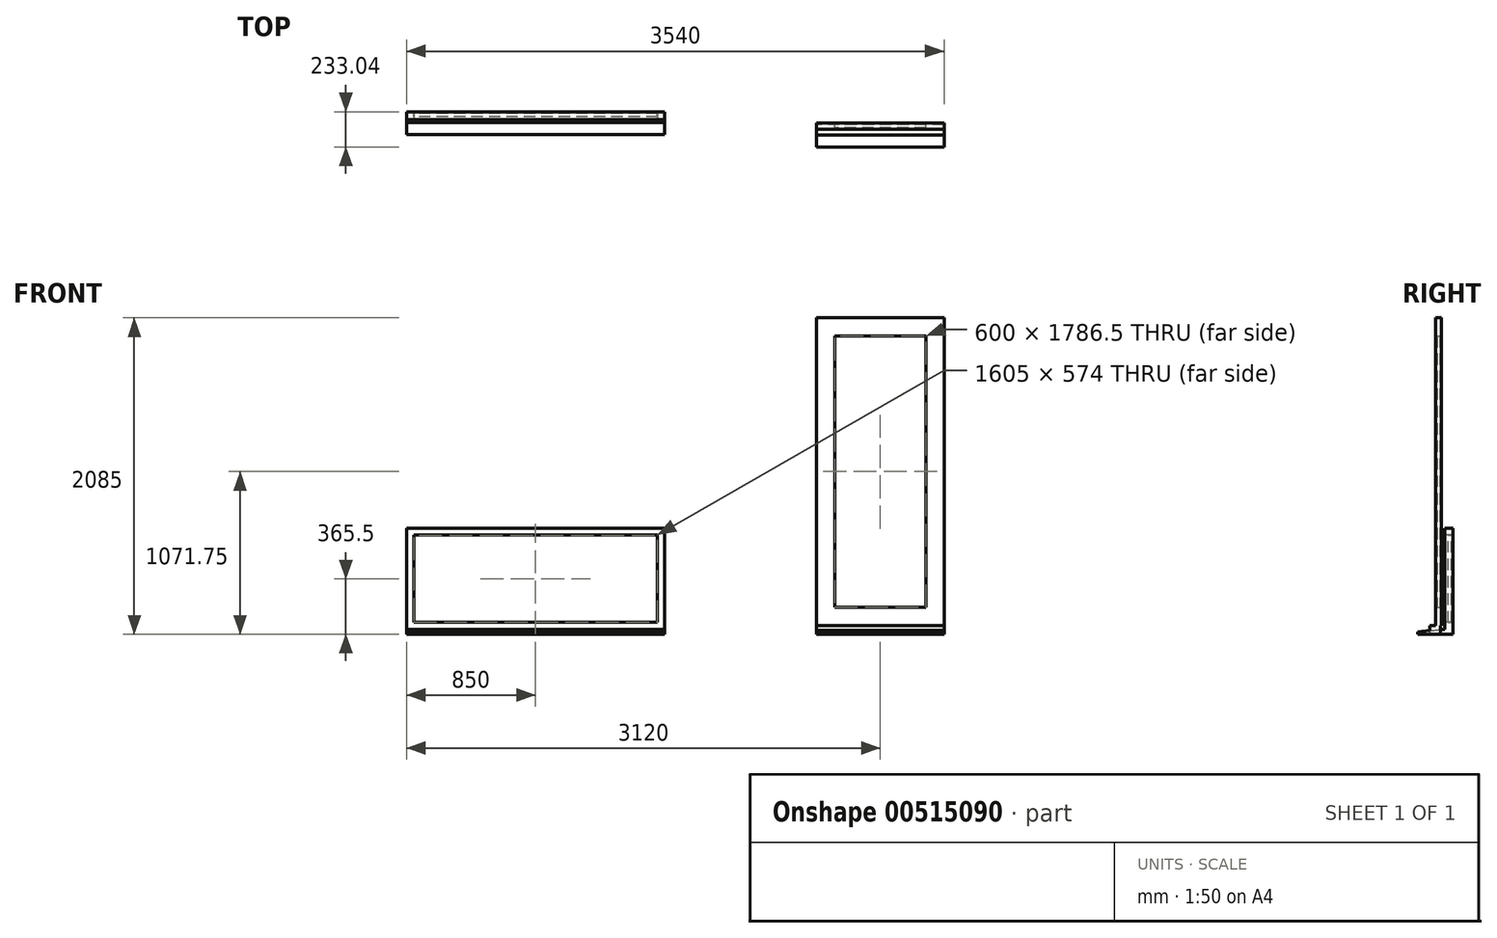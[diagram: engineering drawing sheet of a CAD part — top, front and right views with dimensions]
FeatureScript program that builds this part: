
annotation { "Feature Type Name" : "Feature", "Feature Type Description" : "" }
export const myFeature = defineFeature(function(context is Context, id is Id, definition is map)
    precondition{}
    {
        {
            var Q0;
            Q0=qCreatedBy(makeId("Right.planeOp"),FACE);
            var sketch = newSketch(context, id + "F0", { "sketchPlane" : qUnion([Q0])});
            skLineSegment(sketch, "E0.bottom", {"start": v(83.04, 0) * mm, "end": v(-66.96, 0) * mm});
            skLineSegment(sketch, "E0.top", {"start": v(83.04, 31) * mm, "end": v(-66.96, 31) * mm});
            skLineSegment(sketch, "E0.left", {"start": v(83.04, 0) * mm, "end": v(83.04, 31) * mm});
            skLineSegment(sketch, "E0.right", {"start": v(-66.96, 0) * mm, "end": v(-66.96, 31) * mm});
            skSolve(sketch);
        }
        {
            var Q0;
            Q0=makeQuery(id+"F0.imprint","IMPRINT",FACE,{"disambiguationData":[TD([[makeQuery(id+"F0.imprint","IMPRINT",EDGE,{"derivedFrom":sQuery(id+"F0.wireOp",EDGE,"E0.bottom")}),-1.0]])]});
            extrude(context, id + "F1", {"entities" : qUnion([Q0]), "oppositeDirection" : true, "depth" : 1700 * mm});
        }
        {
            var Q0;
            Q0=makeQuery(id+"F1.opExtrude","SWEPT_FACE",FACE,{"disambiguationData":[OSD([sQuery(id+"F0.wireOp",EDGE,"E0.left")])]});
            var sketch = newSketch(context, id + "F2", { "sketchPlane" : qUnion([Q0])});
            skLineSegment(sketch, "E1.bottom", {"start": v(0, 31) * mm, "end": v(1700, 31) * mm});
            skLineSegment(sketch, "E1.top", {"start": v(0, 700) * mm, "end": v(1700, 700) * mm});
            skLineSegment(sketch, "E1.left", {"start": v(0, 31) * mm, "end": v(0, 700) * mm});
            skLineSegment(sketch, "E1.right", {"start": v(1700, 31) * mm, "end": v(1700, 700) * mm});
            skSolve(sketch);
        }
        {
            var Q0;
            Q0=qCreatedBy(makeId("Right.planeOp"),FACE);
            var sketch = newSketch(context, id + "F3", { "sketchPlane" : qUnion([Q0])});
            skLineSegment(sketch, "E2.bottom", {"start": v(83.04, 31) * mm, "end": v(30.04, 31) * mm});
            skLineSegment(sketch, "E2.top", {"start": v(83.04, 78.5) * mm, "end": v(30.04, 78.5) * mm});
            skLineSegment(sketch, "E2.left", {"start": v(83.04, 31) * mm, "end": v(83.04, 78.5) * mm});
            skLineSegment(sketch, "E2.right", {"start": v(30.04, 31) * mm, "end": v(30.04, 78.5) * mm});
            skSolve(sketch);
        }
        {
            var Q0;
            Q0=makeQuery(id+"F3.imprint","IMPRINT",FACE,{"disambiguationData":[TD([[makeQuery(id+"F3.imprint","IMPRINT",EDGE,{"derivedFrom":sQuery(id+"F3.wireOp",EDGE,"E2.bottom")}),-1.0]])]});
            var Q1;
            Q1=qConstructionFilter(qBodyType(qCreatedBy(id+"F2",EDGE),BodyType.WIRE),ConstructionObject.NO);
            sweep(context, id + "F4", {"operationType" : NewBodyOperationType.ADD, "profiles" : qUnion([Q0]), "path" : qUnion([Q1])});
        }
        {
            var Q0;
            Q0=makeQuery(id+"F4.boolean.opBoolean","MERGE",FACE,{"derivedFrom":[makeQuery(id+"F1.opExtrude","SWEPT_FACE",FACE,{"disambiguationData":[OSD([sQuery(id+"F0.wireOp",EDGE,"E0.left")])]}),makeQuery(id+"F4.opSweep","SWEPT_FACE",FACE,{"disambiguationData":[OSD([sQuery(id+"F2.wireOp",EDGE,"E1.bottom"),sQuery(id+"F3.wireOp",EDGE,"E2.left")])]})]});
            cPlane(context, id + "F5", {"entities" : qUnion([Q0]), "cplaneType" : CPlaneType.OFFSET, "offset" : 10 * mm, "oppositeDirection" : true, "width" : 150 * mm, "height" : 150 * mm});
        }
        {
            var Q0;
            Q0=qCreatedBy(id+"F5.planeOp",FACE);
            var sketch = newSketch(context, id + "F6", { "sketchPlane" : qUnion([Q0])});
            skLineSegment(sketch, "E3.bottom", {"start": v(47.5, 78.5) * mm, "end": v(1652.5, 78.5) * mm});
            skLineSegment(sketch, "E3.top", {"start": v(47.5, 652.5) * mm, "end": v(1652.5, 652.5) * mm});
            skLineSegment(sketch, "E3.left", {"start": v(47.5, 78.5) * mm, "end": v(47.5, 652.5) * mm});
            skLineSegment(sketch, "E3.right", {"start": v(1652.5, 78.5) * mm, "end": v(1652.5, 652.5) * mm});
            skSolve(sketch);
        }
        {
            var Q0;
            Q0=makeQuery(id+"F6.imprint","IMPRINT",FACE,{"disambiguationData":[TD([[makeQuery(id+"F6.imprint","IMPRINT",EDGE,{"derivedFrom":sQuery(id+"F6.wireOp",EDGE,"E3.bottom")}),1.0]])]});
            extrude(context, id + "F7", {"entities" : qUnion([Q0]), "oppositeDirection" : true, "depth" : 22 * mm});
        }
        {
            var Q0;
            Q0=qCreatedBy(makeId("Right.planeOp"),FACE);
            cPlane(context, id + "F8", {"entities" : qUnion([Q0]), "cplaneType" : CPlaneType.OFFSET, "offset" : 1000 * mm, "width" : 150 * mm, "height" : 150 * mm});
        }
        {
            var Q0;
            Q0=qCreatedBy(id+"F8.planeOp",FACE);
            var sketch = newSketch(context, id + "F9", { "sketchPlane" : qUnion([Q0])});
            skLineSegment(sketch, "E4.bottom", {"start": v(0, 0) * mm, "end": v(-150, 0) * mm});
            skLineSegment(sketch, "E4.top", {"start": v(-70, 25) * mm, "end": v(-150, 25) * mm});
            skLineSegment(sketch, "E4.left", {"start": v(0, 0) * mm, "end": v(0, 25) * mm});
            skLineSegment(sketch, "E4.right", {"start": v(-150, 0) * mm, "end": v(-150, 25) * mm});
            skLineSegment(sketch, "E5.top", {"start": v(0, 58.5) * mm, "end": v(-70, 58.5) * mm});
            skLineSegment(sketch, "E5.left", {"start": v(0, 25) * mm, "end": v(0, 58.5) * mm});
            skLineSegment(sketch, "E5.right", {"start": v(-70, 25) * mm, "end": v(-70, 58.5) * mm});
            skSolve(sketch);
        }
        {
            var Q0;
            Q0=makeQuery(id+"F9.imprint","IMPRINT",FACE,{"disambiguationData":[TD([[makeQuery(id+"F9.imprint","IMPRINT",EDGE,{"derivedFrom":sQuery(id+"F9.wireOp",EDGE,"E4.bottom")}),-1.0]])]});
            extrude(context, id + "F10", {"entities" : qUnion([Q0]), "depth" : 840 * mm});
        }
        {
            var Q0;
            Q0=makeQuery(id+"F10.opExtrude","SWEPT_FACE",FACE,{"disambiguationData":[OSD([sQuery(id+"F9.wireOp",EDGE,"E4.left"),sQuery(id+"F9.wireOp",EDGE,"E5.left")])]});
            cPlane(context, id + "F11", {"entities" : qUnion([Q0]), "cplaneType" : CPlaneType.OFFSET, "offset" : 8 * mm, "width" : 150 * mm, "height" : 150 * mm});
        }
        {
            var Q0;
            Q0=qCreatedBy(id+"F11.planeOp",FACE);
            var sketch = newSketch(context, id + "F12", { "sketchPlane" : qUnion([Q0])});
            skLineSegment(sketch, "E6.bottom", {"start": v(-1000, 58.5) * mm, "end": v(-1840, 58.5) * mm});
            skLineSegment(sketch, "E6.top", {"start": v(-1000, 2085) * mm, "end": v(-1840, 2085) * mm});
            skLineSegment(sketch, "E6.left", {"start": v(-1000, 58.5) * mm, "end": v(-1000, 2085) * mm});
            skLineSegment(sketch, "E6.right", {"start": v(-1840, 58.5) * mm, "end": v(-1840, 2085) * mm});
            skLineSegment(sketch, "E7.bottom", {"start": v(-1720, 1965) * mm, "end": v(-1120, 1965) * mm});
            skLineSegment(sketch, "E7.top", {"start": v(-1720, 178.5) * mm, "end": v(-1120, 178.5) * mm});
            skLineSegment(sketch, "E7.left", {"start": v(-1720, 1965) * mm, "end": v(-1720, 178.5) * mm});
            skLineSegment(sketch, "E7.right", {"start": v(-1120, 1965) * mm, "end": v(-1120, 178.5) * mm});
            skSolve(sketch);
        }
        {
            var Q0;
            Q0=makeQuery(id+"F12.imprint","IMPRINT",FACE,{"disambiguationData":[TD([[makeQuery(id+"F12.imprint","IMPRINT",EDGE,{"derivedFrom":sQuery(id+"F12.wireOp",EDGE,"E6.bottom")}),-1.0]])]});
            extrude(context, id + "F13", {"entities" : qUnion([Q0]), "operationType" : NewBodyOperationType.ADD, "oppositeDirection" : true, "depth" : 40 * mm});
        }
        {
            var Q0;
            Q0=makeQuery(id+"F13.opExtrude","CAP_FACE",FACE,{"disambiguationData":[OSD([sQuery(id+"F12.wireOp",EDGE,"E6.bottom"),sQuery(id+"F12.wireOp",EDGE,"E6.top"),sQuery(id+"F12.wireOp",EDGE,"E6.left"),sQuery(id+"F12.wireOp",EDGE,"E6.right"),sQuery(id+"F12.wireOp",EDGE,"E7.bottom"),sQuery(id+"F12.wireOp",EDGE,"E7.top"),sQuery(id+"F12.wireOp",EDGE,"E7.left"),sQuery(id+"F12.wireOp",EDGE,"E7.right")])],"isStart":true});
            cPlane(context, id + "F14", {"entities" : qUnion([Q0]), "cplaneType" : CPlaneType.OFFSET, "offset" : 10 * mm, "oppositeDirection" : true, "width" : 150 * mm, "height" : 150 * mm});
        }
        {
            var Q0;
            Q0=qCreatedBy(id+"F14.planeOp",FACE);
            var sketch = newSketch(context, id + "F15", { "sketchPlane" : qUnion([Q0])});
            skLineSegment(sketch, "E8.bottom", {"start": v(-1720, 1965) * mm, "end": v(-1120, 1965) * mm});
            skLineSegment(sketch, "E8.top", {"start": v(-1720, 178.5) * mm, "end": v(-1120, 178.5) * mm});
            skLineSegment(sketch, "E8.left", {"start": v(-1720, 1965) * mm, "end": v(-1720, 178.5) * mm});
            skLineSegment(sketch, "E8.right", {"start": v(-1120, 1965) * mm, "end": v(-1120, 178.5) * mm});
            skSolve(sketch);
        }
        {
            var Q0;
            Q0=qSketchRegion(id+"F15",true);
            extrude(context, id + "F16", {"entities" : qUnion([Q0]), "oppositeDirection" : true, "depth" : 20 * mm});
        }
        {
            var Q0;
            Q0=makeQuery(id+"F1.opExtrude","SWEPT_EDGE",EDGE,{"disambiguationData":[OSD([sQuery(id+"F0.wireOp",EDGE,"E0.top"),sQuery(id+"F0.wireOp",EDGE,"E0.right")])]});
            chamfer(context, id + "F17", {"entities" : qUnion([Q0]), "chamferType" : ChamferType.TWO_OFFSETS, "width1" : 80 * mm, "oppositeDirection" : false, "width2" : 8 * mm, "tangentPropagation" : true});
        }
        {
            var Q0;
            Q0=makeQuery(id+"F10.opExtrude","SWEPT_EDGE",EDGE,{"disambiguationData":[OSD([sQuery(id+"F9.wireOp",EDGE,"E4.top"),sQuery(id+"F9.wireOp",EDGE,"E4.right")])]});
            chamfer(context, id + "F18", {"entities" : qUnion([Q0]), "chamferType" : ChamferType.TWO_OFFSETS, "width1" : 8 * mm, "oppositeDirection" : false, "width2" : 80 * mm, "tangentPropagation" : true});
        }
    });
